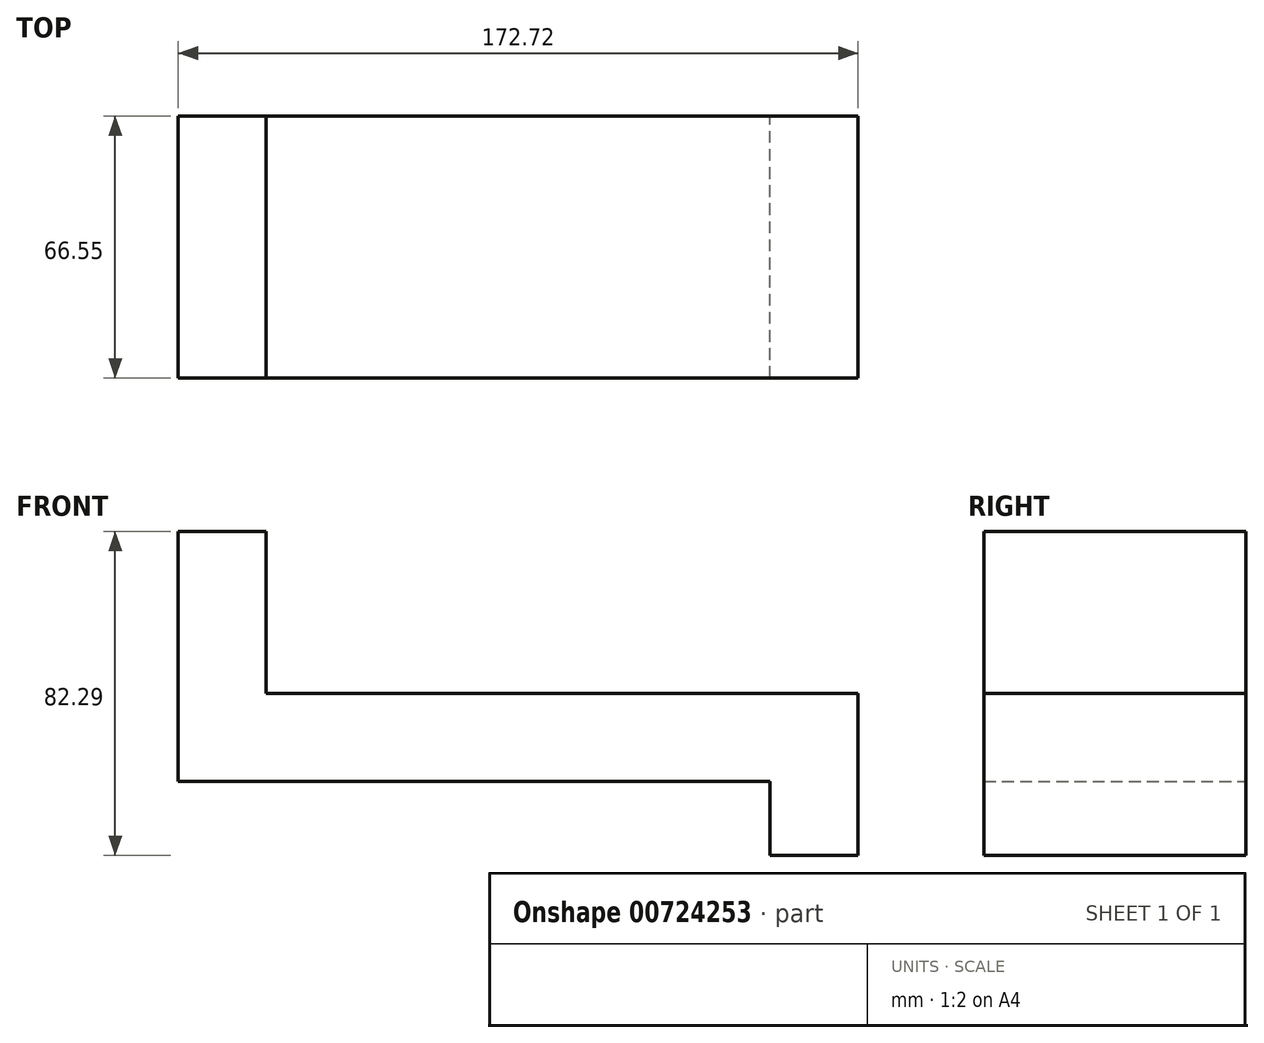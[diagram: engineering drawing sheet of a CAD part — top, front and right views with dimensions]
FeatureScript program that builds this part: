
annotation { "Feature Type Name" : "Feature", "Feature Type Description" : "" }
export const myFeature = defineFeature(function(context is Context, id is Id, definition is map)
    precondition{}
    {
        {
            var Q0;
            Q0=qCreatedBy(makeId("Front.planeOp"),FACE);
            var sketch = newSketch(context, id + "F0", { "sketchPlane" : qUnion([Q0])});
            skLineSegment(sketch, "E0", {"start": v(-76.17, 69.66) * mm, "end": v(-76.17, 6.16) * mm});
            skLineSegment(sketch, "E1", {"start": v(-76.17, 6.16) * mm, "end": v(74.2, 6.16) * mm});
            skLineSegment(sketch, "E2", {"start": v(74.2, 6.16) * mm, "end": v(74.2, -12.63) * mm});
            skLineSegment(sketch, "E3", {"start": v(74.2, -12.63) * mm, "end": v(96.55, -12.63) * mm});
            skLineSegment(sketch, "E4", {"start": v(96.55, -12.63) * mm, "end": v(96.55, 28.52) * mm});
            skLineSegment(sketch, "E5", {"start": v(96.55, 28.52) * mm, "end": v(-53.82, 28.52) * mm});
            skLineSegment(sketch, "E6", {"start": v(-53.82, 28.52) * mm, "end": v(-53.82, 69.66) * mm});
            skLineSegment(sketch, "E7", {"start": v(-53.82, 69.66) * mm, "end": v(-76.17, 69.66) * mm});
            skSolve(sketch);
        }
        {
            var Q0;
            Q0=makeQuery(id+"F0.imprint","IMPRINT",FACE,{"disambiguationData":[TD([[makeQuery(id+"F0.imprint","IMPRINT",EDGE,{"derivedFrom":sQuery(id+"F0.wireOp",EDGE,"E0")}),1.0]])]});
            extrude(context, id + "F1", {"entities" : qUnion([Q0]), "depth" : 66.55 * mm, "offsetDistance" : 25.4 * mm});
        }
    });
